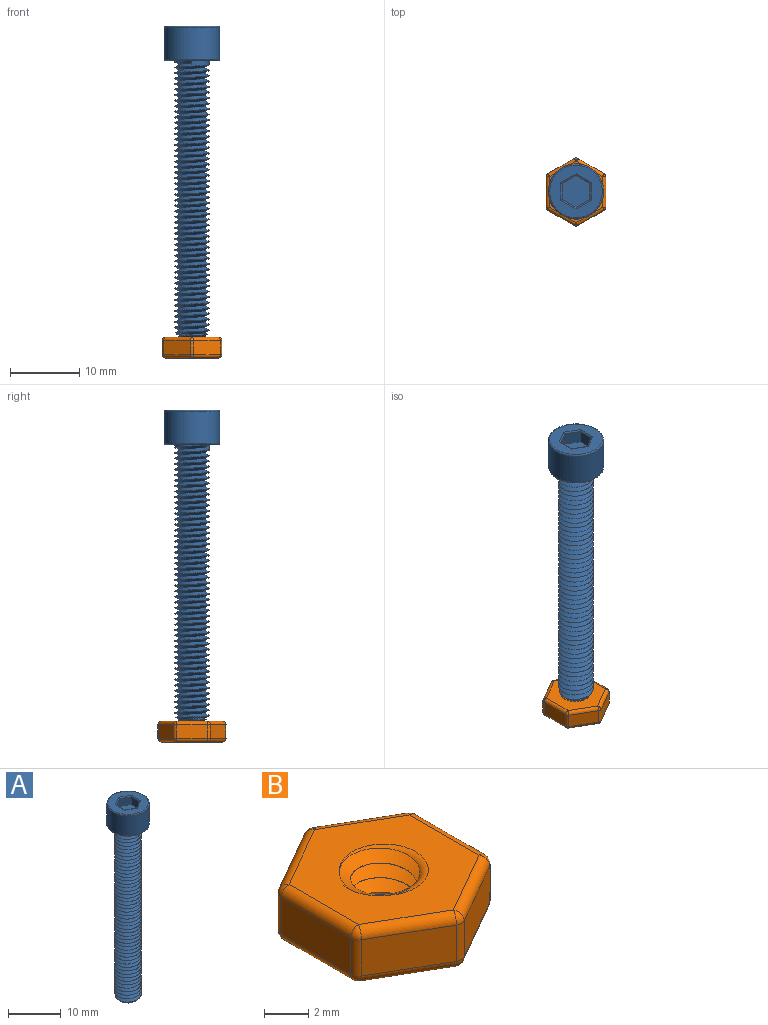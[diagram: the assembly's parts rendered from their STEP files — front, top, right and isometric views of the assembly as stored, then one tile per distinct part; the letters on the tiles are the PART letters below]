
ASSEMBLY  parts=2 mates=1
PART A: 24 faces, bbox 8.7x8.7x45.4 mm
  f0: cone r=2.5mm half-angle=45deg, axis (0,0,1), area 6.6mm2, adj f2,f3,f22,f23
  f1: plane 7.6x7.6mm, normal (0,0,1), area 28.7mm2, adj f13,f14,f15,f16,f17,f18,f20
  f2: cylinder r=2.5mm len=39.3mm, axis (0,0,-1), area 362.2mm2, adj f0,f5,f21,f22,f23
  f3: plane 3.6x3.6mm, normal (0,0,-1), area 10.2mm2, adj f0
  f4: cylinder r=4mm len=8mm, axis (0,0,-1), area 115.6mm2, adj f19,f20
  f5: plane 7.6x7.6mm, normal (0,0,-1), area 25.7mm2, adj f2,f19
  f6: plane 1.99x1.8mm, normal (0.5,-0.87,0), area 4.1mm2, adj f7,f11,f12,f14
  f7: plane 2.3x1.8mm, normal (1,0,0), area 4.1mm2, adj f6,f8,f12,f13
  f8: plane 1.99x1.8mm, normal (0.5,0.87,0), area 4.1mm2, adj f7,f9,f12,f15
  f9: plane 1.99x1.8mm, normal (-0.5,0.87,0), area 4.1mm2, adj f8,f10,f12,f17
  f10: plane 2.3x1.8mm, normal (-1,0,0), area 4.1mm2, adj f9,f11,f12,f18
  f11: plane 1.99x1.8mm, normal (-0.5,-0.87,0), area 4.1mm2, adj f6,f10,f12,f16
  f12: plane 4.6x3.98mm, normal (0,0,1), area 13.7mm2, adj f6,f7,f8,f9,f10,f11
  f13: cylinder r=0.2mm len=2.53mm, axis (0,1,0), area 0.8mm2, adj f1,f7,f14,f15
  f14: cylinder r=0.2mm len=2.29mm, axis (0.87,0.5,0), area 0.8mm2, adj f1,f6,f13,f16
  f15: cylinder r=0.2mm len=2.29mm, axis (-0.87,0.5,0), area 0.8mm2, adj f1,f8,f13,f17
  f16: cylinder r=0.2mm len=2.29mm, axis (0.87,-0.5,0), area 0.8mm2, adj f1,f11,f14,f18
  f17: cylinder r=0.2mm len=2.29mm, axis (-0.87,-0.5,0), area 0.8mm2, adj f1,f9,f15,f18
  f18: cylinder r=0.2mm len=2.53mm, axis (0,-1,0), area 0.8mm2, adj f1,f10,f16,f17
  f19: torus R=3.8mm, axis (0,0,1), area 7.8mm2, adj f4,f5
  f20: torus R=3.8mm, axis (0,0,1), area 7.8mm2, adj f1,f4
  f21: plane 0.79x0.68mm, normal (-1,0,0), area 0.3mm2, adj f2,f22,f23
  f22: bspline ~40x5.77mm, area 528.8mm2, adj f0,f2,f21,f23
  f23: bspline ~40x5.77mm, area 523.8mm2, adj f0,f2,f21,f22
PART B: 44 faces, bbox 8.9x10.1x3.8 mm
  f0: cylinder r=1.5mm len=3mm, axis (0,0,-1), area 0.7mm2, adj f39,f40,f41,f42,f43
  f1: plane 3.83x2.21mm, normal (0.5,-0.87,0), area 8.8mm2, adj f27,f32,f35,f38
  f2: plane 4.42x2mm, normal (1,0,0), area 8.8mm2, adj f24,f33,f34,f38
  f3: plane 3.83x2.21mm, normal (0.5,0.87,0), area 8.8mm2, adj f14,f23,f24,f25
  f4: plane 3.83x2.21mm, normal (-0.5,0.87,0), area 8.8mm2, adj f9,f13,f14,f15
  f5: plane 4.42x2mm, normal (-1,0,0), area 8.8mm2, adj f9,f12,f16,f17
  f6: plane 3.83x2.21mm, normal (-0.5,-0.87,0), area 8.8mm2, adj f17,f22,f26,f27
  f7: plane 8.88x7.69mm, normal (0,0,1), area 37.9mm2, adj f12,f13,f22,f23,f32,f33,f40,f42
  f8: plane 8.85x7.66mm, normal (0,0,-1), area 38.3mm2, adj f15,f16,f25,f26,f34,f35,f39
  f9: cylinder r=0.5mm len=2mm, axis (0,0,-1), area 1mm2, adj f4,f5,f10,f11
  f10: sphere r=0.5mm, area 0.3mm2, adj f9,f12,f13
  f11: sphere r=0.5mm, area 0.3mm2, adj f9,f15,f16
  f12: cylinder r=0.5mm len=4.42mm, axis (0,1,0), area 3.5mm2, adj f5,f7,f10,f18
  f13: cylinder r=0.5mm len=4.08mm, axis (0.87,0.5,0), area 3.5mm2, adj f4,f7,f10,f19
  f14: cylinder r=0.5mm len=2mm, axis (0,0,-1), area 1mm2, adj f3,f4,f19,f20
  f15: cylinder r=0.5mm len=4.08mm, axis (-0.87,-0.5,0), area 3.5mm2, adj f4,f8,f11,f20
  f16: cylinder r=0.5mm len=4.42mm, axis (0,-1,0), area 3.5mm2, adj f5,f8,f11,f21
  f17: cylinder r=0.5mm len=2mm, axis (0,0,-1), area 1mm2, adj f5,f6,f18,f21
  f18: sphere r=0.5mm, area 0.3mm2, adj f12,f17,f22
  f19: sphere r=0.5mm, area 0.4mm2, adj f13,f14,f23
  f20: sphere r=0.5mm, area 0.4mm2, adj f14,f15,f25
  f21: sphere r=0.5mm, area 0.3mm2, adj f16,f17,f26
  f22: cylinder r=0.5mm len=4.08mm, axis (-0.87,0.5,0), area 3.5mm2, adj f6,f7,f18,f28
  f23: cylinder r=0.5mm len=4.08mm, axis (0.87,-0.5,0), area 3.5mm2, adj f3,f7,f19,f29
  f24: cylinder r=0.5mm len=2mm, axis (0,0,-1), area 1mm2, adj f2,f3,f29,f30
  f25: cylinder r=0.5mm len=4.08mm, axis (-0.87,0.5,0), area 3.5mm2, adj f3,f8,f20,f30
  f26: cylinder r=0.5mm len=4.08mm, axis (0.87,-0.5,0), area 3.5mm2, adj f6,f8,f21,f31
  f27: cylinder r=0.5mm len=2mm, axis (0,0,-1), area 1mm2, adj f1,f6,f28,f31
  f28: sphere r=0.5mm, area 0.3mm2, adj f22,f27,f32
  f29: sphere r=0.5mm, area 0.2mm2, adj f23,f24,f33
  f30: sphere r=0.5mm, area 0.2mm2, adj f24,f25,f34
  f31: sphere r=0.5mm, area 0.4mm2, adj f26,f27,f35
  f32: cylinder r=0.5mm len=4.08mm, axis (-0.87,-0.5,0), area 3.5mm2, adj f1,f7,f28,f36
  f33: cylinder r=0.5mm len=4.42mm, axis (0,-1,0), area 3.5mm2, adj f2,f7,f29,f36
  f34: cylinder r=0.5mm len=4.42mm, axis (0,1,0), area 3.5mm2, adj f2,f8,f30,f37
  f35: cylinder r=0.5mm len=4.08mm, axis (0.87,0.5,0), area 3.5mm2, adj f1,f8,f31,f37
  f36: sphere r=0.5mm, area 0.3mm2, adj f32,f33,f38
  f37: sphere r=0.5mm, area 0.3mm2, adj f34,f35,f38
  f38: cylinder r=0.5mm len=2mm, axis (0,0,-1), area 1mm2, adj f1,f2,f36,f37
  f39: torus R=2mm, axis (0,0,1), area 6.9mm2, adj f0,f8,f41,f42
  f40: torus R=2mm, axis (0,0,1), area 2.4mm2, adj f0,f7,f42,f43
  f41: plane 0.9x0.9mm, normal (-1,0,0), area 0.2mm2, adj f0,f39,f42,f43
  f42: bspline ~5.04x4.37mm, area 30.9mm2, adj f0,f7,f39,f40,f41,f43
  f43: bspline ~5.04x4.37mm, area 26.9mm2, adj f0,f7,f40,f41,f42
PLACE A t=(-4.89,-2.15,0.5)mm fixed
PLACE B rot(axis=(0,0,1),0deg) t=(-4.89,-2.15,-22.5)mm
MATE cylindrical B.f0 <-> A.f0  axis (0,0,1) through (-4.89,-2.15,-19.5)mm
